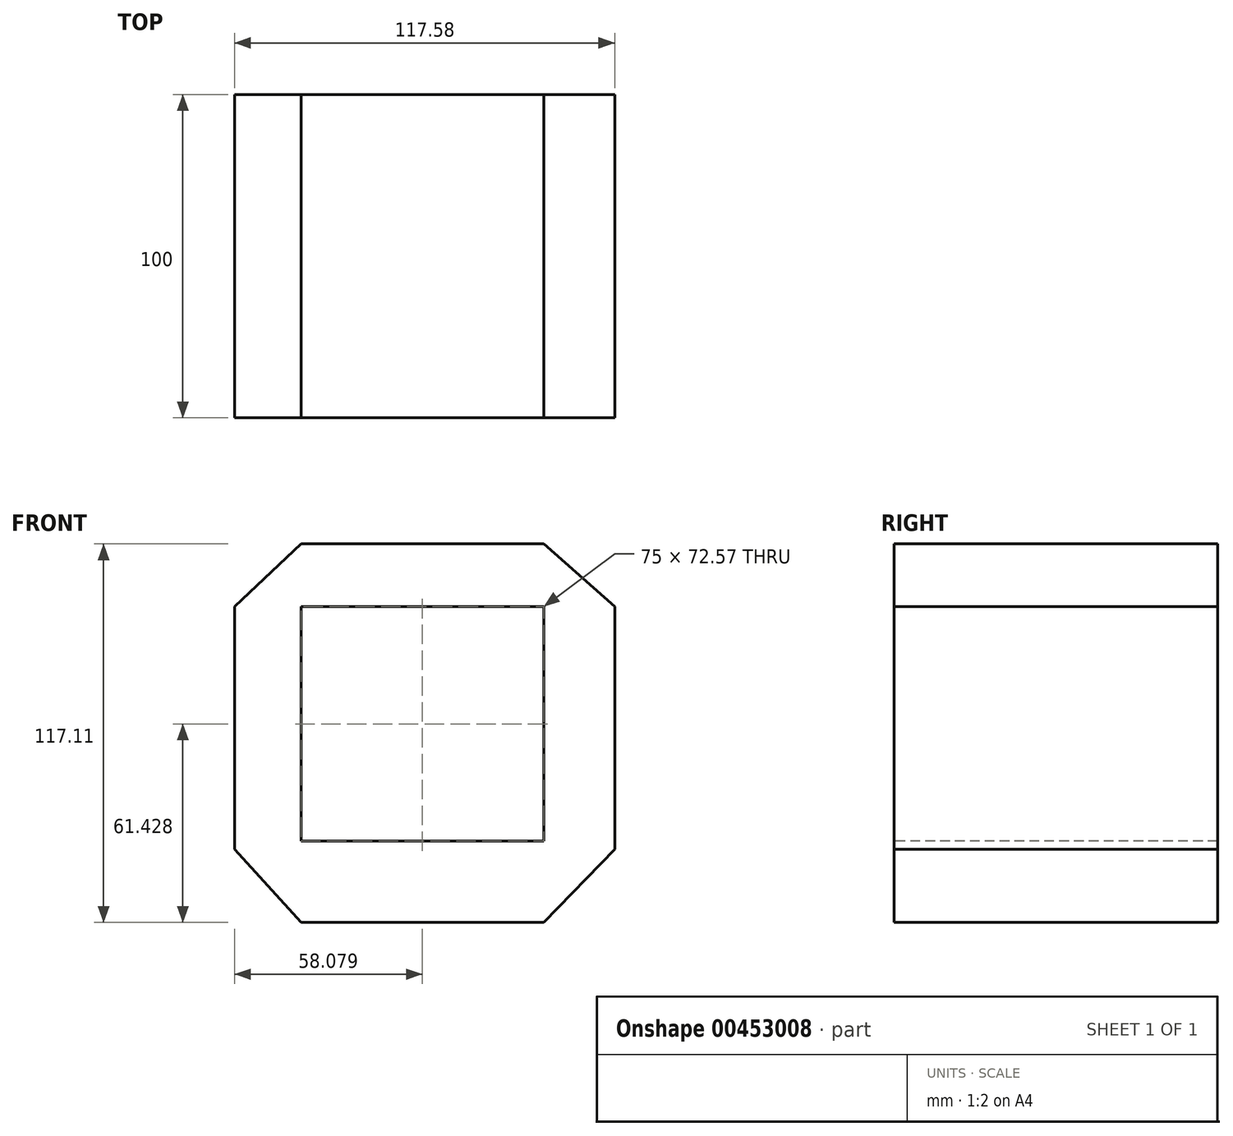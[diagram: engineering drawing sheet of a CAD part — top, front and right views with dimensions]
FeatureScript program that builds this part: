
annotation { "Feature Type Name" : "Feature", "Feature Type Description" : "" }
export const myFeature = defineFeature(function(context is Context, id is Id, definition is map)
    precondition{}
    {
        {
            var Q0;
            Q0=qCreatedBy(makeId("Front.planeOp"),FACE);
            var sketch = newSketch(context, id + "F0", { "sketchPlane" : qUnion([Q0])});
            skLineSegment(sketch, "E0", {"start": v(-55.5, 48.78) * mm, "end": v(-55.5, -26.22) * mm});
            skLineSegment(sketch, "E1", {"start": v(-55.5, -26.22) * mm, "end": v(-34.91, -48.93) * mm});
            skLineSegment(sketch, "E2", {"start": v(-34.91, -48.93) * mm, "end": v(40.09, -48.93) * mm});
            skLineSegment(sketch, "E3", {"start": v(40.09, -48.93) * mm, "end": v(62.1, -26.22) * mm});
            skLineSegment(sketch, "E4", {"start": v(62.1, -26.22) * mm, "end": v(62.1, 48.78) * mm});
            skLineSegment(sketch, "E5", {"start": v(62.1, 48.78) * mm, "end": v(40.09, 68.18) * mm});
            skLineSegment(sketch, "E6", {"start": v(40.09, 68.18) * mm, "end": v(-34.91, 68.18) * mm});
            skLineSegment(sketch, "E7", {"start": v(-34.91, 68.18) * mm, "end": v(-55.5, 48.78) * mm});
            skLineSegment(sketch, "E8", {"start": v(-34.91, 48.78) * mm, "end": v(-34.91, -23.79) * mm});
            skLineSegment(sketch, "E9", {"start": v(-34.91, -23.79) * mm, "end": v(40.09, -23.79) * mm});
            skLineSegment(sketch, "E10", {"start": v(40.09, -23.79) * mm, "end": v(40.09, 48.78) * mm});
            skLineSegment(sketch, "E11", {"start": v(40.09, 48.78) * mm, "end": v(-34.91, 48.78) * mm});
            skSolve(sketch);
        }
        {
            var Q0;
            Q0 = qSketchRegion(id + "F0", true);
            extrude(context, id + "F1", {"entities" : qUnion([Q0]), "oppositeDirection" : true, "depth" : 50 * mm, "hasSecondDirection" : true, "secondDirectionOppositeDirection" : false, "secondDirectionDepth" : 50 * mm});
        }
    });
